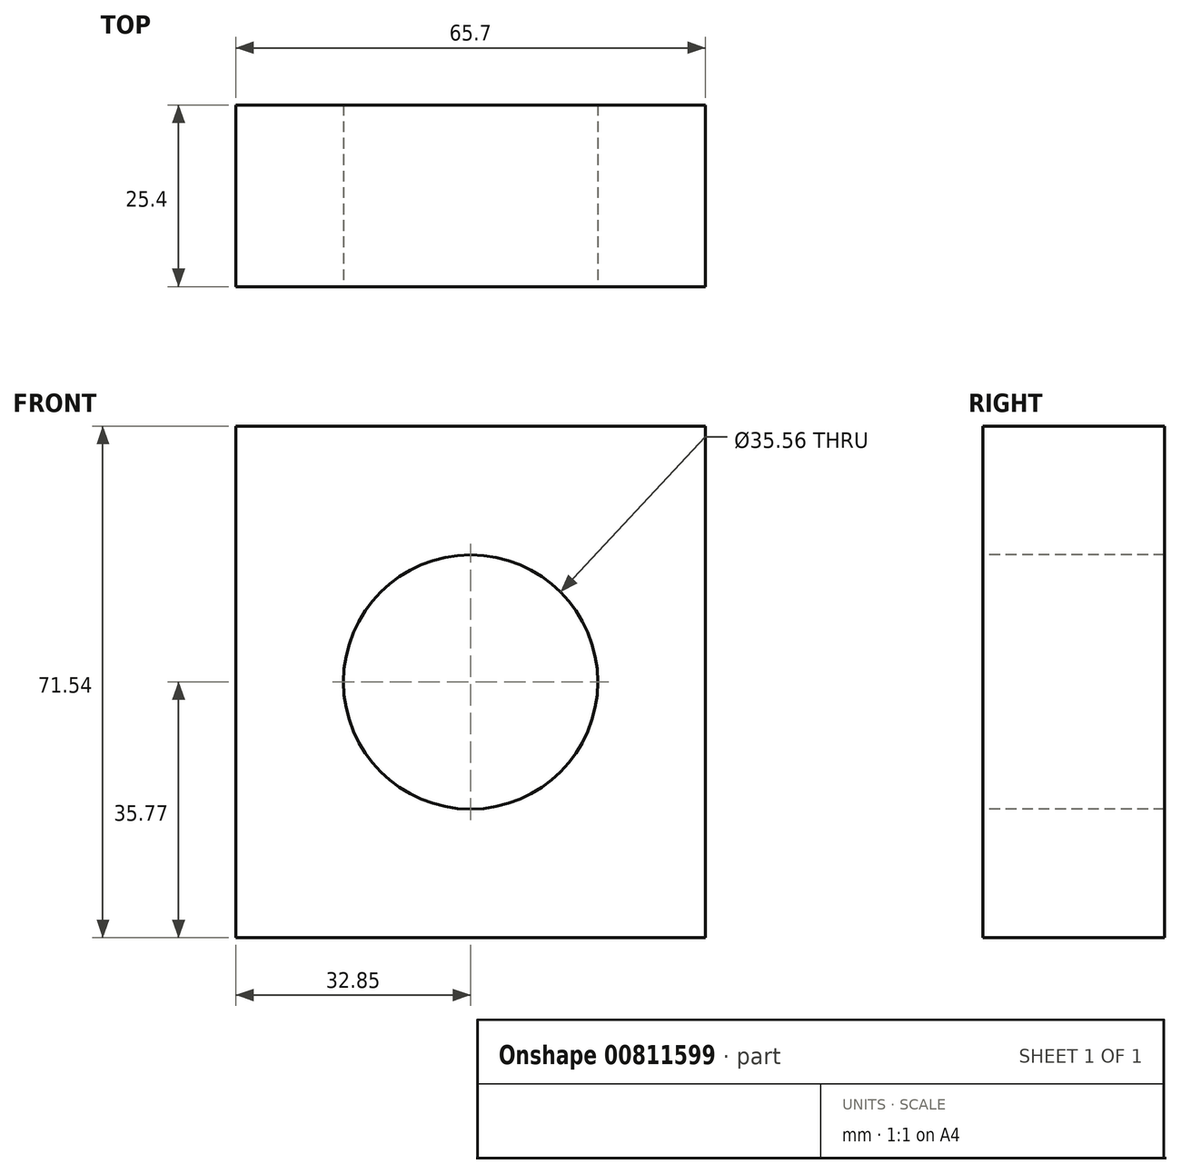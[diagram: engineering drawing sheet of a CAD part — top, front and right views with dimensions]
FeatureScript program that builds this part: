
annotation { "Feature Type Name" : "Feature", "Feature Type Description" : "" }
export const myFeature = defineFeature(function(context is Context, id is Id, definition is map)
    precondition{}
    {
        {
            var Q0;
            Q0=qCreatedBy(makeId("Front.planeOp"),FACE);
            var sketch = newSketch(context, id + "F0", { "sketchPlane" : qUnion([Q0])});
            skLineSegment(sketch, "E0.bottom", {"start": v(-32.85, -35.77) * mm, "end": v(32.85, -35.77) * mm});
            skLineSegment(sketch, "E0.top", {"start": v(-32.85, 35.77) * mm, "end": v(32.85, 35.77) * mm});
            skLineSegment(sketch, "E0.left", {"start": v(-32.85, -35.77) * mm, "end": v(-32.85, 35.77) * mm});
            skLineSegment(sketch, "E0.right", {"start": v(32.85, -35.77) * mm, "end": v(32.85, 35.77) * mm});
            skPoint(sketch, "E0.middle", {"position": v(0, 0) * mm});
            skSolve(sketch);
        }
        {
            var Q0;
            Q0 = qSketchRegion(id + "F0", true);
            extrude(context, id + "F1", {"entities" : qUnion([Q0]), "depth" : 25.4 * mm, "offsetDistance" : 25.4 * mm});
        }
        {
            var Q0;
            Q0=makeQuery(id+"F1.opExtrude","CAP_FACE",FACE,{"disambiguationData":[OSD([sQuery(id+"F0.wireOp",EDGE,"E0.bottom"),sQuery(id+"F0.wireOp",EDGE,"E0.top"),sQuery(id+"F0.wireOp",EDGE,"E0.left"),sQuery(id+"F0.wireOp",EDGE,"E0.right")])],"isStart":false});
            var sketch = newSketch(context, id + "F2", { "sketchPlane" : qUnion([Q0])});
            skCircle(sketch, "E1", {"center": v(0, 0) * mm, "radius": 18.03 * mm});
            skSolve(sketch);
        }
        {
            var Q0;
            Q0=sQuery(id+"F2.wireOp",VERTEX,"E1.center");
            var Q1;
            Q1=makeQuery(id+"F1.opExtrude","SWEPT_BODY",BODY,{"disambiguationData":[OSD([sQuery(id+"F0.wireOp",EDGE,"E0.bottom"),sQuery(id+"F0.wireOp",EDGE,"E0.top"),sQuery(id+"F0.wireOp",EDGE,"E0.left"),sQuery(id+"F0.wireOp",EDGE,"E0.right")])]});
            hole(context, id + "F3", {"style" : HoleStyle.SIMPLE, "endStyle" : HoleEndStyle.THROUGH, "holeDiameter" : 35.56 * mm, "majorDiameter" : 6.35 * mm, "isTappedThrough" : true, "tappedDepth" : 12.7 * mm, "tapClearance" : 3, "locations" : qUnion([Q0]), "scope" : qUnion([Q1])});
        }
    });
